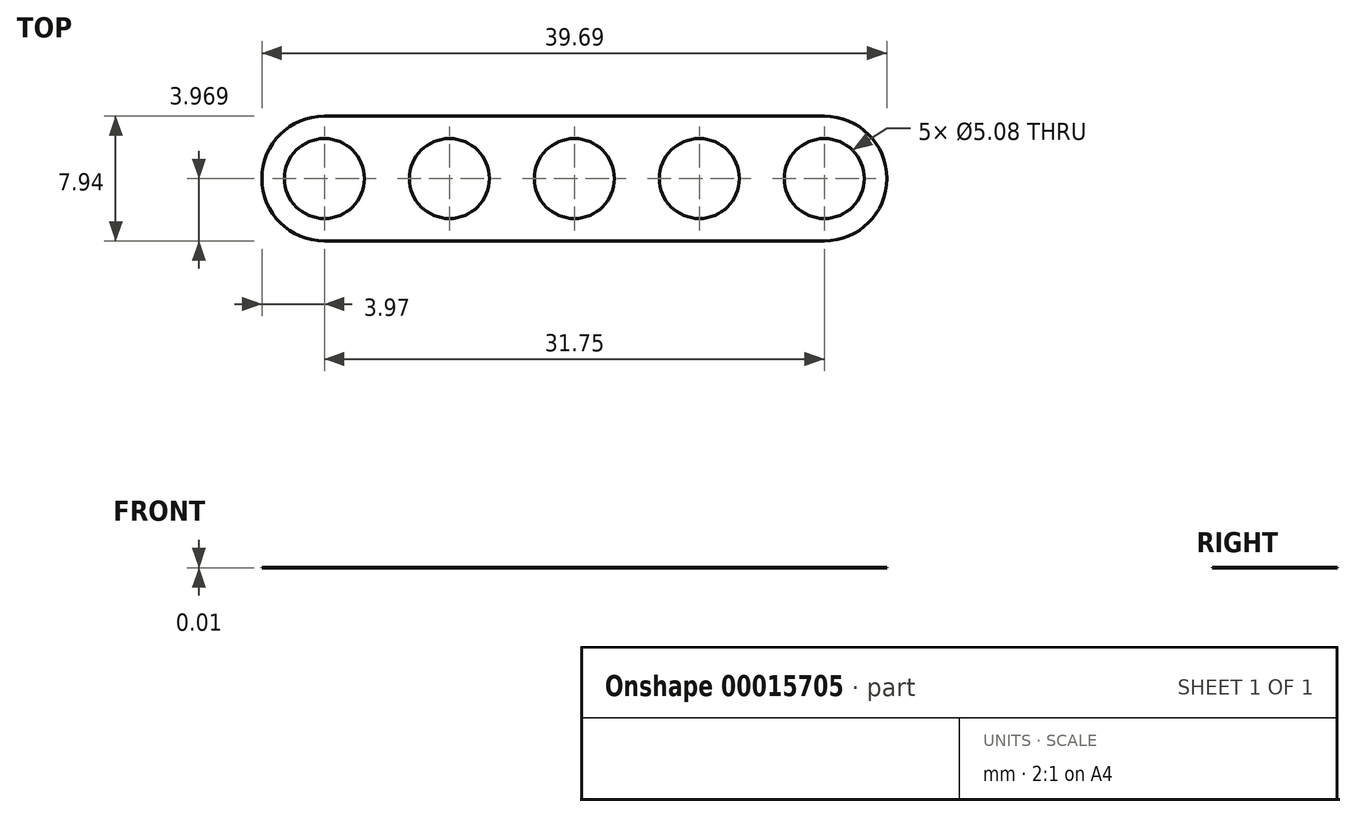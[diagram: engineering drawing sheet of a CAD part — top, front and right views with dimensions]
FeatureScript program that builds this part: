
annotation { "Feature Type Name" : "Feature", "Feature Type Description" : "" }
export const myFeature = defineFeature(function(context is Context, id is Id, definition is map)
    precondition{}
    {
        {
            var Q0;
            Q0=qCreatedBy(makeId("Top.planeOp"),FACE);
            var sketch = newSketch(context, id + "F0", { "sketchPlane" : qUnion([Q0])});
            skLineSegment(sketch, "E0.bottom", {"start": v(0, 0) * mm, "end": v(31.75, 0) * mm});
            skLineSegment(sketch, "E0.top", {"start": v(0, 7.94) * mm, "end": v(31.75, 7.94) * mm});
            skLineSegment(sketch, "E0.left", {"start": v(0, 0) * mm, "end": v(0, 7.94) * mm});
            skLineSegment(sketch, "E0.right", {"start": v(31.75, 0) * mm, "end": v(31.75, 7.94) * mm});
            skLineSegment(sketch, "E1", {"start": v(23.81, 3.97) * mm, "end": v(31.75, 3.97) * mm});
            skCircle(sketch, "E2", {"center": v(31.75, 3.97) * mm, "radius": 2.54 * mm});
            skCircle(sketch, "E3", {"center": v(23.81, 3.97) * mm, "radius": 2.54 * mm});
            skCircle(sketch, "E4", {"center": v(0, 3.97) * mm, "radius": 2.54 * mm});
            skArc(sketch, "E5", {"start": v(31.75, 0) * mm, "mid": v(35.72, 3.97) * mm, "end": v(31.75, 7.94) * mm});
            skArc(sketch, "E6", {"start": v(0, 7.94) * mm, "mid": v(-3.97, 3.97) * mm, "end": v(0, 0) * mm});
            skLineSegment(sketch, "E7", {"start": v(0, 3.97) * mm, "end": v(7.94, 3.97) * mm});
            skLineSegment(sketch, "E8", {"start": v(7.94, 3.97) * mm, "end": v(15.87, 3.97) * mm});
            skLineSegment(sketch, "E9", {"start": v(15.87, 3.97) * mm, "end": v(23.81, 3.97) * mm});
            skCircle(sketch, "E10", {"center": v(7.94, 3.97) * mm, "radius": 2.54 * mm});
            skCircle(sketch, "E11", {"center": v(15.87, 3.97) * mm, "radius": 2.54 * mm});
            skSolve(sketch);
        }
        {
            var Q0;
            Q0=qSketchRegion(id+"F0",true);
            extrude(context, id + "F1", {"entities" : qUnion([Q0]), "depth" : 5 / 406.4 * mm});
        }
    });
